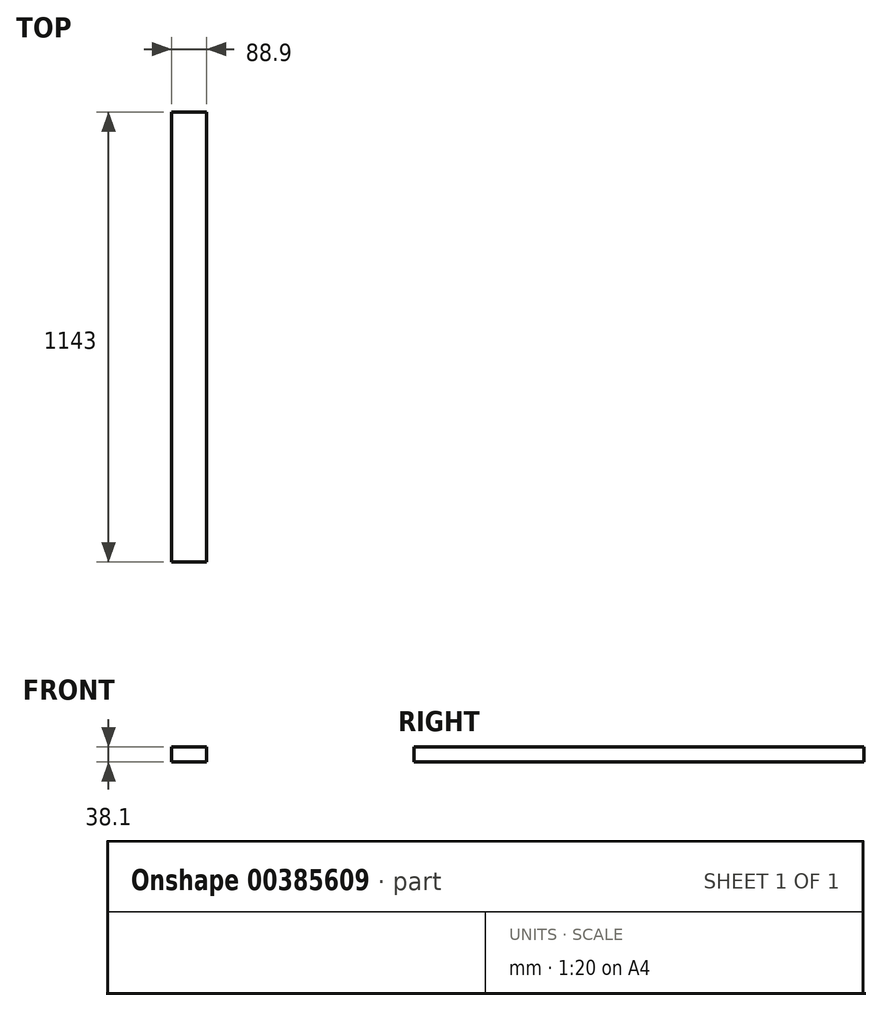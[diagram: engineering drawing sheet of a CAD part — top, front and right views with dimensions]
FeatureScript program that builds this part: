
annotation { "Feature Type Name" : "Feature", "Feature Type Description" : "" }
export const myFeature = defineFeature(function(context is Context, id is Id, definition is map)
    precondition{}
    {
        {
            var Q0;
            Q0=qCreatedBy(makeId("Front.planeOp"),FACE);
            var sketch = newSketch(context, id + "F0", { "sketchPlane" : qUnion([Q0])});
            skLineSegment(sketch, "E0.bottom", {"start": v(0, 0) * mm, "end": v(88.9, 0) * mm});
            skLineSegment(sketch, "E0.top", {"start": v(0, 38.1) * mm, "end": v(88.9, 38.1) * mm});
            skLineSegment(sketch, "E0.left", {"start": v(0, 0) * mm, "end": v(0, 38.1) * mm});
            skLineSegment(sketch, "E0.right", {"start": v(88.9, 0) * mm, "end": v(88.9, 38.1) * mm});
            skSolve(sketch);
        }
        {
            var Q0;
            Q0=makeQuery(id+"F0.imprint","IMPRINT",FACE,{"disambiguationData":[TD([[makeQuery(id+"F0.imprint","IMPRINT",EDGE,{"derivedFrom":sQuery(id+"F0.wireOp",EDGE,"E0.bottom")}),1.0]])]});
            extrude(context, id + "F1", {"entities" : qUnion([Q0]), "depth" : 1143 * mm});
        }
    });
